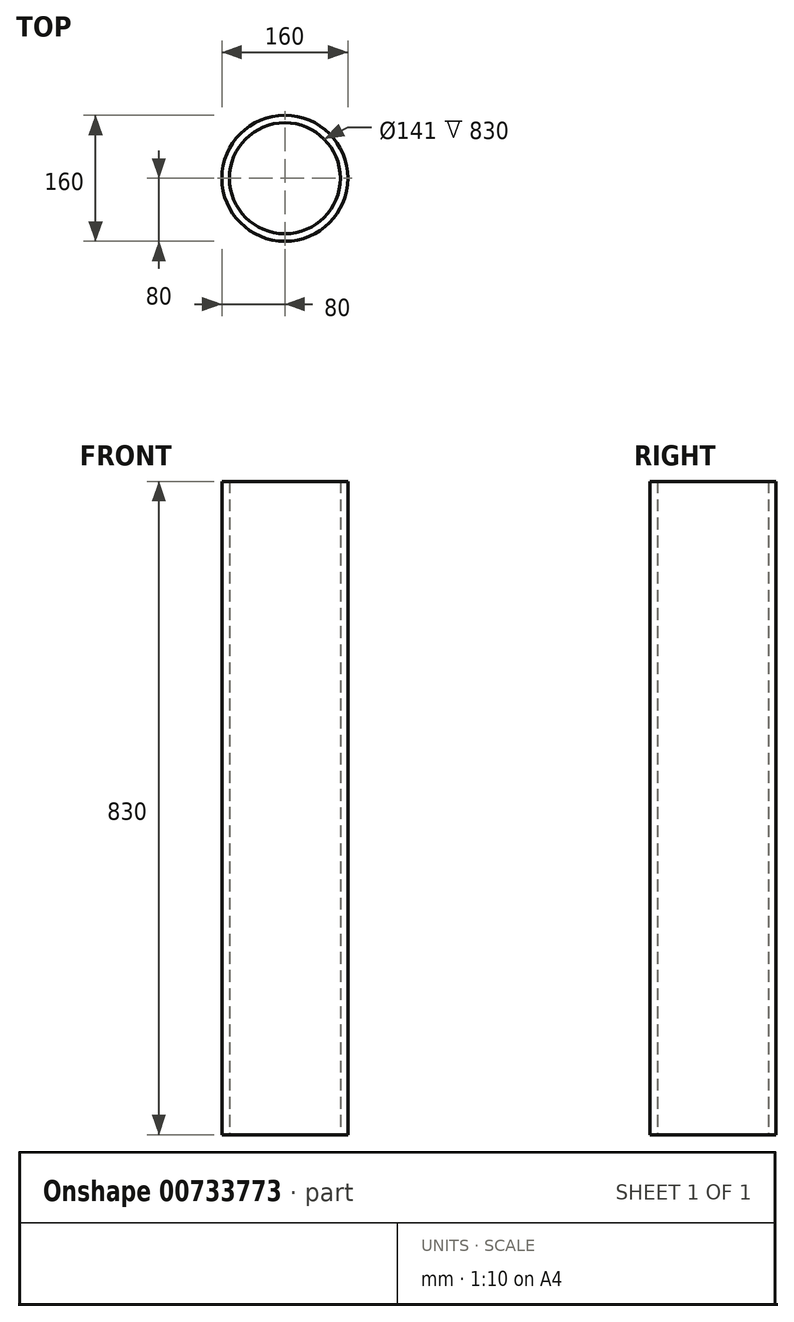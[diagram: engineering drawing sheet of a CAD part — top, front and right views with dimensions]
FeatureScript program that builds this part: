
annotation { "Feature Type Name" : "Feature", "Feature Type Description" : "" }
export const myFeature = defineFeature(function(context is Context, id is Id, definition is map)
    precondition{}
    {
        {
            var Q0;
            Q0=qCreatedBy(makeId("Top.planeOp"),FACE);
            var sketch = newSketch(context, id + "F0", { "sketchPlane" : qUnion([Q0])});
            skCircle(sketch, "E0", {"center": v(0, 0) * mm, "radius": 70.5 * mm});
            skCircle(sketch, "E1", {"center": v(0, 0) * mm, "radius": 80 * mm});
            skSolve(sketch);
        }
        {
            var Q0;
            Q0=makeQuery(id+"F0.imprint","IMPRINT",FACE,{"disambiguationData":[TD([[makeQuery(id+"F0.imprint","IMPRINT",EDGE,{"derivedFrom":sQuery(id+"F0.wireOp",EDGE,"E0")}),-1.0]])]});
            extrude(context, id + "F1", {"entities" : qUnion([Q0]), "depth" : 830 * mm, "offsetDistance" : 25 * mm});
        }
    });
